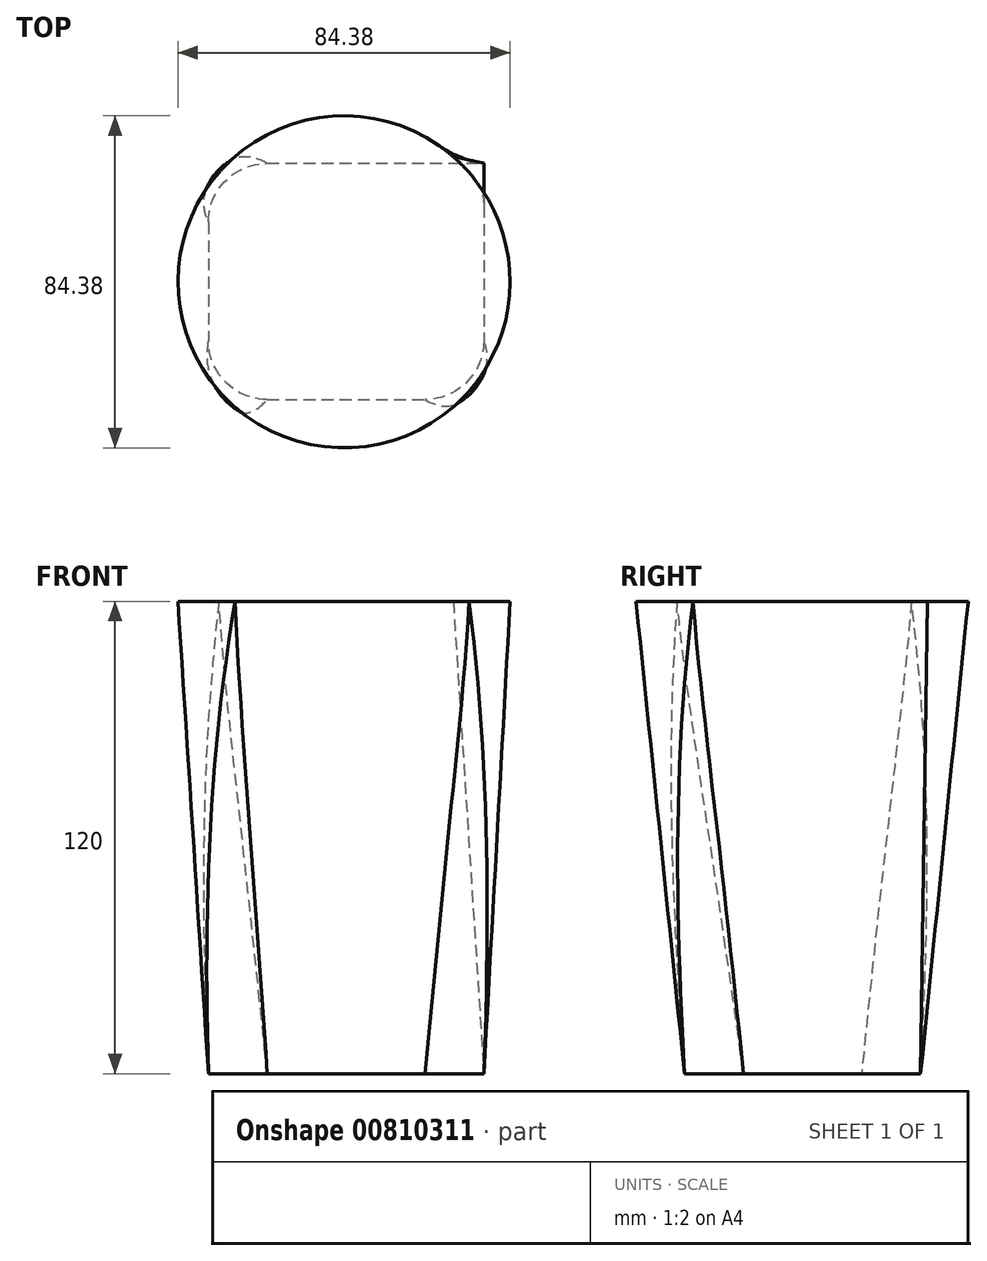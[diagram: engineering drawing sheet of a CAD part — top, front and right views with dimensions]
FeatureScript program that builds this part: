
annotation { "Feature Type Name" : "Feature", "Feature Type Description" : "" }
export const myFeature = defineFeature(function(context is Context, id is Id, definition is map)
    precondition{}
    {
        {
            var Q0;
            Q0=qCreatedBy(makeId("Top.planeOp"),FACE);
            cPlane(context, id + "F0", {"entities" : qUnion([Q0]), "cplaneType" : CPlaneType.OFFSET, "offset" : 120 * mm, "width" : 150 * mm, "height" : 150 * mm});
        }
        {
            var Q0;
            Q0=qCreatedBy(makeId("Top.planeOp"),FACE);
            var sketch = newSketch(context, id + "F1", { "sketchPlane" : qUnion([Q0])});
            skLineSegment(sketch, "E0.bottom", {"start": v(-47.74, 23.93) * mm, "end": v(22.26, 23.93) * mm});
            skLineSegment(sketch, "E0.top", {"start": v(-47.74, -36.07) * mm, "end": v(22.26, -36.07) * mm});
            skLineSegment(sketch, "E0.left", {"start": v(-47.74, 23.93) * mm, "end": v(-47.74, -36.07) * mm});
            skLineSegment(sketch, "E0.right", {"start": v(22.26, 23.93) * mm, "end": v(22.26, -36.07) * mm});
            skSolve(sketch);
        }
        {
            var Q0;
            Q0=qCreatedBy(id+"F0.planeOp",FACE);
            var sketch = newSketch(context, id + "F2", { "sketchPlane" : qUnion([Q0])});
            skCircle(sketch, "E1", {"center": v(-13.26, -6.17) * mm, "radius": 42.2 * mm});
            skSolve(sketch);
        }
        {
            var Q0;
            Q0=makeQuery(id+"F2.imprint","IMPRINT",FACE,{"disambiguationData":[TD([[makeQuery(id+"F2.imprint","IMPRINT",EDGE,{"derivedFrom":sQuery(id+"F2.wireOp",EDGE,"E1")}),1.0]])]});
            var Q1;
            Q1=makeQuery(id+"F1.imprint","IMPRINT",FACE,{"disambiguationData":[TD([[makeQuery(id+"F1.imprint","IMPRINT",EDGE,{"derivedFrom":sQuery(id+"F1.wireOp",EDGE,"E0.bottom")}),-1.0]])]});
            loft(context, id + "F3", {"sheetProfilesArray" : [{ "sheetProfileEntities" : qUnion([Q0]) }, { "sheetProfileEntities" : qUnion([Q1]) }]});
        }
        {
            var Q0;
            Q0=makeQuery(id+"F3.opLoft","SWEPT_EDGE",EDGE,{"disambiguationData":[OSD([sQuery(id+"F1.wireOp",EDGE,"E0.bottom"),sQuery(id+"F1.wireOp",EDGE,"E0.top"),sQuery(id+"F1.wireOp",EDGE,"E0.right"),sQuery(id+"F2.wireOp",EDGE,"E1")])]});
            var Q1;
            Q1=makeQuery(id+"F3.opLoft","SWEPT_EDGE",EDGE,{"disambiguationData":[OSD([sQuery(id+"F1.wireOp",EDGE,"E0.bottom"),sQuery(id+"F1.wireOp",EDGE,"E0.left"),sQuery(id+"F1.wireOp",EDGE,"E0.right"),sQuery(id+"F2.wireOp",EDGE,"E1")])]});
            var Q2;
            Q2=makeQuery(id+"F3.opLoft","SWEPT_EDGE",EDGE,{"disambiguationData":[OSD([sQuery(id+"F1.wireOp",EDGE,"E0.bottom"),sQuery(id+"F1.wireOp",EDGE,"E0.left")])]});
            var Q3;
            Q3=makeQuery(id+"F3.opLoft","SWEPT_EDGE",EDGE,{"disambiguationData":[OSD([sQuery(id+"F1.wireOp",EDGE,"E0.top"),sQuery(id+"F1.wireOp",EDGE,"E0.left"),sQuery(id+"F1.wireOp",EDGE,"E0.right"),sQuery(id+"F2.wireOp",EDGE,"E1")])]});
            fillet(context, id + "F4", {"entities" : qUnion([Q0, Q1, Q2, Q3]), "radius" : 15 * mm, "tangentPropagation" : true, "allowEdgeOverflow" : false});
        }
        {
            var Q0;
            Q0=qCreatedBy(makeId("Right.planeOp"),FACE);
            cPlane(context, id + "F5", {"entities" : qUnion([Q0]), "cplaneType" : CPlaneType.OFFSET, "offset" : 17 * mm, "width" : 150 * mm, "height" : 150 * mm});
        }
    });
